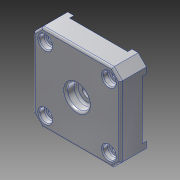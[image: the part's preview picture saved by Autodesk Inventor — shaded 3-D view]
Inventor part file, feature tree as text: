
AUTODESK INVENTOR PART (.ipt)
format: ipt  version: 2016 (Build 200138000, 138)  size: 226,816 bytes
history: native  units: mm
features: hole x4, extrude x3, fillet x3, sketch x3, pattern_linear x2
ambient origin geometry x8: Origin, YZ Plane, XZ Plane, XY Plane, X Axis, Y Axis, Z Axis, Center Point
bodies: Solid1 (feature_tree)
feature tree (15):
  extrude  "Extrusion1"  Depth=42.3mm
  extrude  "Extrusion2"  Depth=10.5mm
  extrude  "Extrusion3"  Depth=10.5mm TaperAngle=0.0deg
  hole  "Hole1"  [1 undecoded]
  hole  "Hole2"  [1 undecoded]
  pattern_linear  "Rectangular Pattern1"  Spacing1=21.15mm  [1 undecoded]
  hole  "Hole3"  [1 undecoded]
  hole  "Hole4"  [1 undecoded]
  pattern_linear  "Rectangular Pattern2"  Count1=2 Spacing1=31.0mm
  fillet  "Fillet1"  Radius=21.15mm
  fillet  "Fillet2"  Radius=5.65mm
  fillet  "Fillet3"  Radius=20.0mm
  sketch  "Sketch1"  dims[d0=42.3mm d1=42.3mm]
  sketch  "Sketch2"  dims[d2=10.5mm d3=0.0mm d4=5.657mm]
  sketch  "Sketch3"  dims[d5=135.0deg d6=10.5mm d7=0.0mm d8=2.121mm d9=2.121mm d10=0.0mm d11=21.15mm d12=21.15mm d13=5.0mm d14=6.0mm d15=4.0mm d16=2.0mm d17=90.0deg d18=8.0mm d19=20.594885mm d20=5.65mm d21=5.65mm d22=3.0mm d23=6.0mm d24=4.0mm d25=2.0mm d26=90.0deg d27=8.0mm d28=20.594885mm d29=20.0mm d31=31.0mm d32=20.0mm d34=31.0mm d35=21.15mm d36=21.15mm d37=11.0mm d38=6.0mm d39=4.0mm d40=2.0mm d41=90.0deg d42=5.0mm d43=0.0mm d44=5.65mm d45=5.65mm d46=6.2mm d47=6.0mm d48=4.0mm d49=2.0mm d50=90.0deg d51=3.0mm d52=0.0mm d53=20.0mm d55=31.0mm d56=20.0mm d58=31.0mm d59=1.0mm d60=0.5mm d61=1.0mm]
note: 5 required parameter values undecoded (feature->parameter linkage not recoverable at this tier; creation-order binding heuristic only, values carry confidence <= 0.55)
